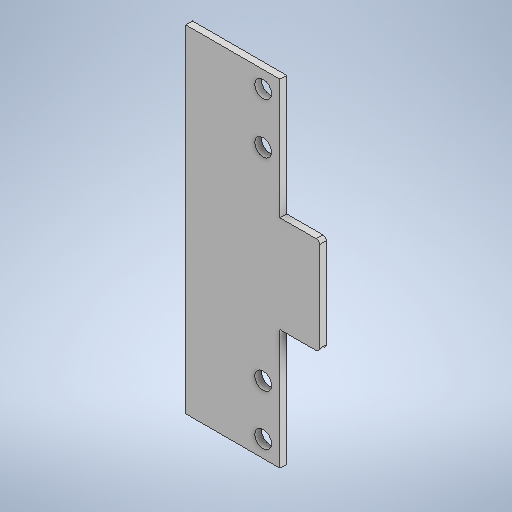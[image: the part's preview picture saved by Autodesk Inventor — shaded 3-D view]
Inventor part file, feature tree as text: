
AUTODESK INVENTOR PART (.ipt)
format: ipt  version: 2025 (Build 290162010, 162A)  size: 306,176 bytes
history: native  units: mm
features: sketch x2, other x2, sheet_metal_op x1, hole x1, fillet x1, projected_geometry x1
ambient origin geometry x8: Origin, YZ Plane, XZ Plane, XY Plane, X Axis, Y Axis, Z Axis, Center Point
bodies: Solid1 (feature_tree)
feature tree (8):
  sheet_metal_op  "Face1"
  hole  "Hole1"  [1 undecoded]
  fillet  "Fillet1"  Radius=112.0mm
  sketch  "Sketch1"  dims[d2=8.0mm]
  other  "Plate1"
  sketch  "Sketch2"  dims[d3=20.0mm d4=6.0mm d5=4.0mm d6=2.0mm d7=90.0deg d8=8.0mm d9=20.594885mm d16=112.0mm d17=400.0mm d19=20.0mm d20=20.0mm d21=360.0mm d22=120.0mm d23=120.0mm d24=47.0mm d25=115.0mm d26=4.0mm]
  projected_geometry  "Projected Loop1"
  other  "Definition1"
note: 1 required parameter value undecoded (feature->parameter linkage not recoverable at this tier; creation-order binding heuristic only, values carry confidence <= 0.55)
